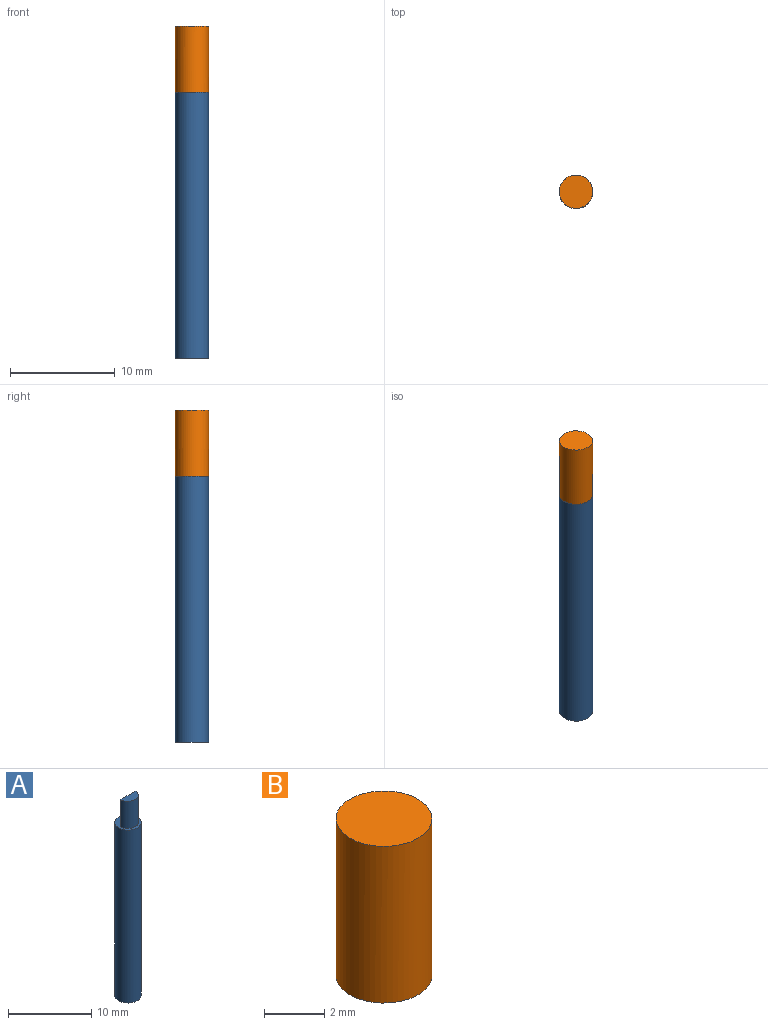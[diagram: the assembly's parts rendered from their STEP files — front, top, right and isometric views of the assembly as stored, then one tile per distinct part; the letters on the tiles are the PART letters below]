
ASSEMBLY  parts=2 mates=1
PART A: 9 faces, bbox 3.2x3.2x29.4 mm
  f0: cylinder r=1.59mm len=25.4mm, axis (0,0,-1), area 253.4mm2, adj f1,f2
  f1: plane 3.18x3.18mm, normal (0,0,1), area 5.5mm2, adj f0,f3,f4
  f2: plane 3.18x3.18mm, normal (0,0,-1), area 5.4mm2, adj f0,f6,f7
  f3: plane 4x2.54mm, normal (0,1,0), area 10.2mm2, adj f1,f4,f5
  f4: cylinder r=1.27mm len=4mm, axis (0,0,-1), area 15.6mm2, adj f1,f3,f5
  f5: plane 2.54x1.22mm, normal (0,0,1), area 2.4mm2, adj f3,f4
  f6: plane 6x2.54mm, normal (0,-1,0), area 15.2mm2, adj f2,f7,f8
  f7: cylinder r=1.27mm len=6mm, axis (0,0,-1), area 23.9mm2, adj f2,f6,f8
  f8: plane 2.54x1.27mm, normal (0,0,-1), area 2.5mm2, adj f6,f7
PART B: 6 faces, bbox 3.2x3.2x6.4 mm
  f0: plane 2.54x1.27mm, normal (0,0,-1), area 2.5mm2, adj f1,f2
  f1: plane 5x2.54mm, normal (0,-1,0), area 12.7mm2, adj f0,f2,f3
  f2: cylinder r=1.27mm len=5mm, axis (0,0,-1), area 19.9mm2, adj f0,f1,f3
  f3: plane 3.18x3.18mm, normal (0,0,-1), area 5.4mm2, adj f1,f2,f4
  f4: cylinder r=1.59mm len=6.35mm, axis (0,0,-1), area 63.3mm2, adj f3,f5
  f5: plane 3.18x3.18mm, normal (0,0,1), area 7.9mm2, adj f4
PLACE A t=(-4.38,0.48,1.62)mm
PLACE B t=(-4.38,0.48,27.02)mm
MATE parallel B.f4 <-> A.f0  axis (0,0,-1) through (-4.38,0.48,27.02)mm
